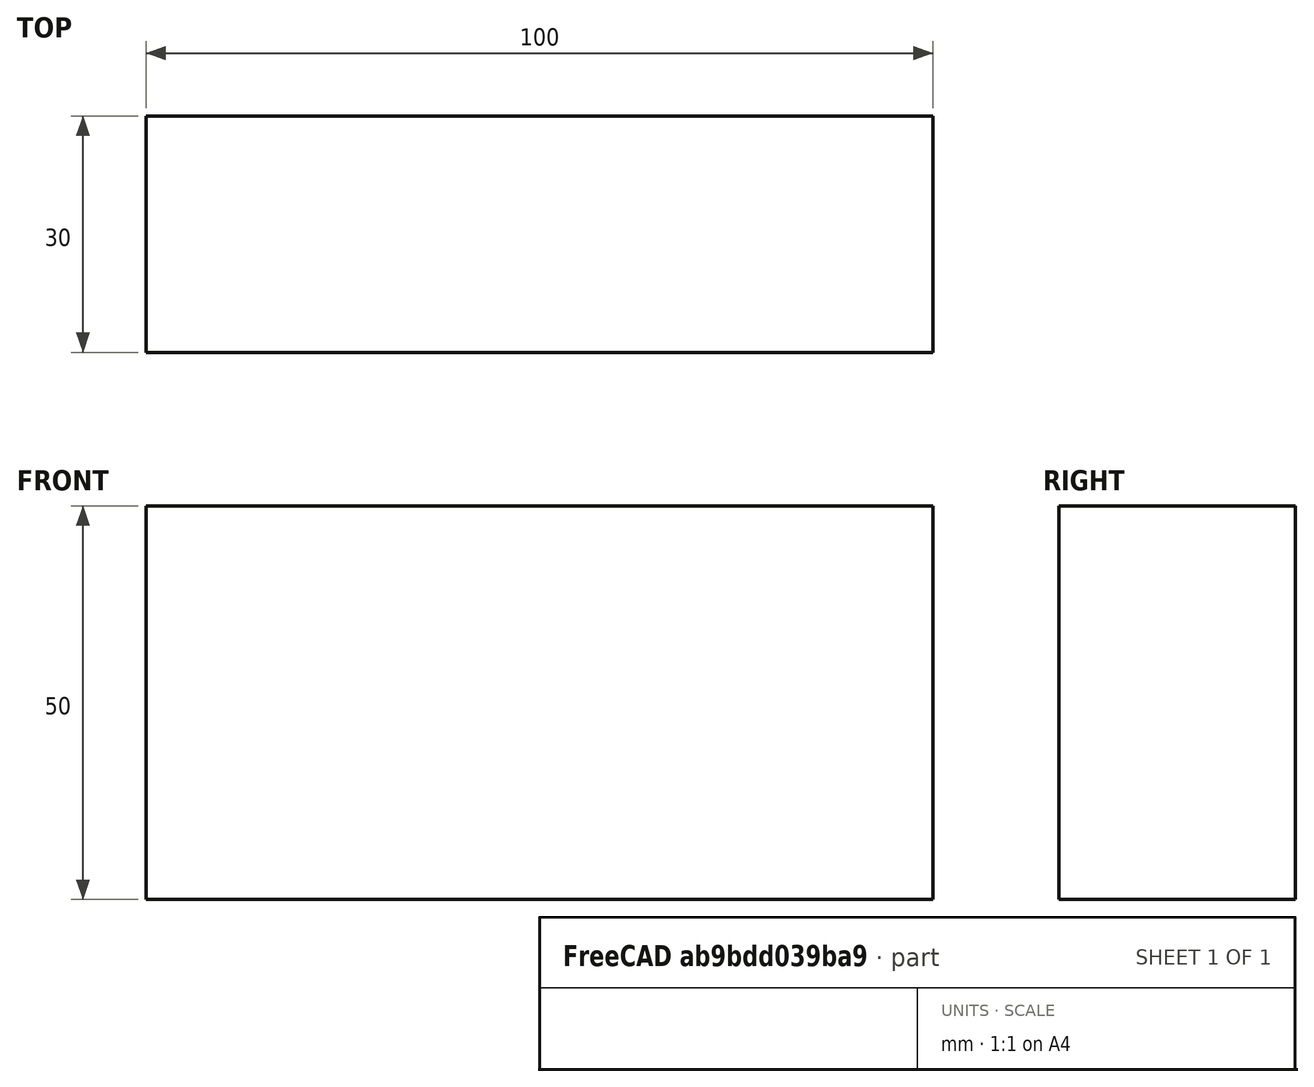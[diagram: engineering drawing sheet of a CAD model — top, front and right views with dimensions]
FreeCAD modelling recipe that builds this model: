
FCSTD DOCUMENT  (FreeCAD 0.15R4671 (Git))
Label: Flat Bar 100x30 EN10058 S235JR
License: All rights reserved
LicenseURL: http://en.wikipedia.org/wiki/All_rights_reserved
objects: Sketcher::SketchObject×1, Part::Extrusion×1
note: 2 computed .brp shape members not serialized (recipe doc carries the construction recipe); baked Part::Feature solids carry a one-line shape summary decoded from their .brp

FEATURE [Sketcher::SketchObject] Sketch
  sketch-geometry (4):
    g0: LineSegment StartX=-50 StartY=-15 StartZ=0 EndX=50 EndY=-15 EndZ=0
    g1: LineSegment StartX=50 StartY=-15 StartZ=0 EndX=50 EndY=15 EndZ=0
    g2: LineSegment StartX=50 StartY=15 StartZ=0 EndX=-50 EndY=15 EndZ=0
    g3: LineSegment StartX=-50 StartY=15 StartZ=0 EndX=-50 EndY=-15 EndZ=0
  constraints (12):
    c: Coincident(g0,g1)
    c: Coincident(g1,g2)
    c: Coincident(g2,g3)
    c: Coincident(g3,g0)
    c: Horizontal(g0)
    c: Horizontal(g2)
    c: Vertical(g1)
    c: Vertical(g3)
    c: Symmetric(g1,g2,g-2)
    c: Symmetric(g0,g1,g-1)
    c: DistanceY(g1) = 30
    c: DistanceX(g0) = 100
FEATURE [Part::Extrusion] Extrude  label="Flat Bar 100x30 EN10058 S235JR"
  Base = -> Sketch
  Dir = (0,0,50)
  Solid = true
